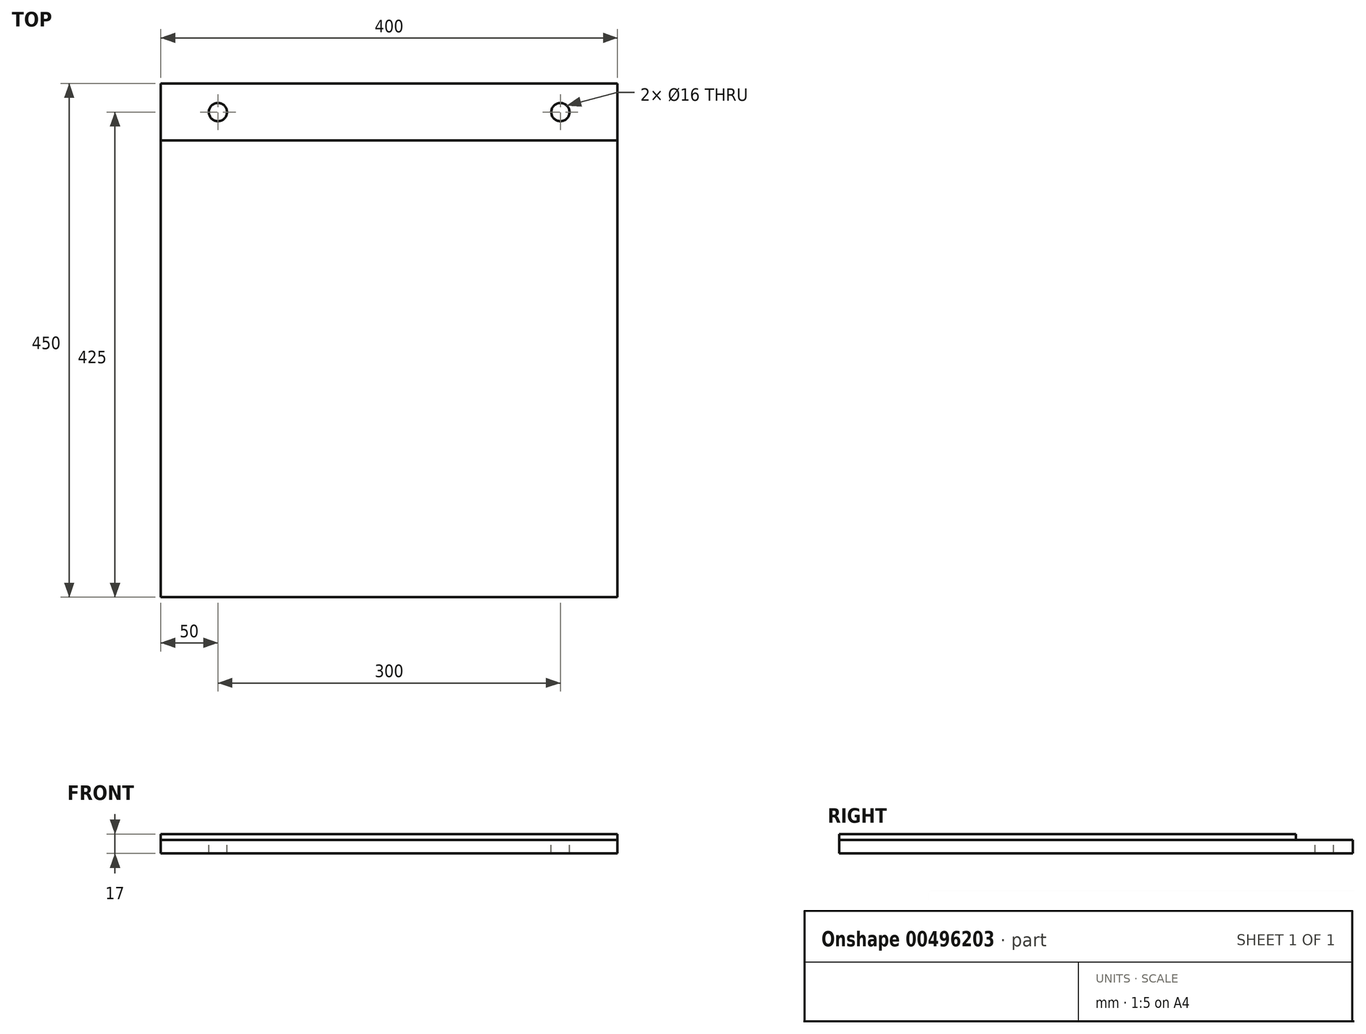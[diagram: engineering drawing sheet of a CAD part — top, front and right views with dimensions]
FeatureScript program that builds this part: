
annotation { "Feature Type Name" : "Feature", "Feature Type Description" : "" }
export const myFeature = defineFeature(function(context is Context, id is Id, definition is map)
    precondition{}
    {
        {
            var Q0;
            Q0=qCreatedBy(makeId("Top.planeOp"),FACE);
            var sketch = newSketch(context, id + "F0", { "sketchPlane" : qUnion([Q0])});
            skLineSegment(sketch, "E0.bottom", {"start": v(0, 0) * mm, "end": v(-400, 0) * mm});
            skLineSegment(sketch, "E0.top", {"start": v(0, 400) * mm, "end": v(-400, 400) * mm});
            skLineSegment(sketch, "E0.left", {"start": v(0, 0) * mm, "end": v(0, 400) * mm});
            skLineSegment(sketch, "E0.right", {"start": v(-400, 0) * mm, "end": v(-400, 400) * mm});
            skSolve(sketch);
        }
        {
            var Q0;
            Q0=makeQuery(id+"F0.imprint","IMPRINT",FACE,{"disambiguationData":[TD([[makeQuery(id+"F0.imprint","IMPRINT",EDGE,{"derivedFrom":sQuery(id+"F0.wireOp",EDGE,"E0.bottom")}),-1.0]])]});
            extrude(context, id + "F1", {"entities" : qUnion([Q0]), "depth" : 5 * mm});
        }
        {
            var Q0;
            Q0=makeQuery(id+"F1.opExtrude","CAP_FACE",FACE,{"disambiguationData":[OSD([sQuery(id+"F0.wireOp",EDGE,"E0.bottom"),sQuery(id+"F0.wireOp",EDGE,"E0.top"),sQuery(id+"F0.wireOp",EDGE,"E0.left"),sQuery(id+"F0.wireOp",EDGE,"E0.right")])],"isStart":true});
            var sketch = newSketch(context, id + "F2", { "sketchPlane" : qUnion([Q0])});
            skLineSegment(sketch, "E1.top", {"start": v(0, -450) * mm, "end": v(-400, -450) * mm});
            skLineSegment(sketch, "E1.left", {"start": v(0, -400) * mm, "end": v(0, -450) * mm});
            skLineSegment(sketch, "E1.right", {"start": v(-400, -400) * mm, "end": v(-400, -450) * mm});
            skLineSegment(sketch, "E2", {"start": v(-400, -425) * mm, "end": v(0, -425) * mm, "construction": true});
            skLineSegment(sketch, "E3", {"start": v(-350, -450) * mm, "end": v(-350, -400) * mm, "construction": true});
            skLineSegment(sketch, "E4", {"start": v(-50, -450) * mm, "end": v(-50, -400) * mm, "construction": true});
            skCircle(sketch, "E5", {"center": v(-350, -425) * mm, "radius": 8 * mm});
            skCircle(sketch, "E6", {"center": v(-50, -425) * mm, "radius": 8 * mm});
            skLineSegment(sketch, "E7", {"start": v(0, -400) * mm, "end": v(0, 0) * mm});
            skLineSegment(sketch, "E8", {"start": v(0, 0) * mm, "end": v(-400, 0) * mm});
            skLineSegment(sketch, "E9", {"start": v(-400, 0) * mm, "end": v(-400, -400) * mm});
            skSolve(sketch);
        }
        {
            var Q0;
            Q0=makeQuery(id+"F2.imprint","IMPRINT",FACE,{"disambiguationData":[TD([[makeQuery(id+"F2.imprint","IMPRINT",EDGE,{"derivedFrom":sQuery(id+"F2.wireOp",EDGE,"E1.top")}),-1.0]])]});
            var Q1;
            Q1=makeQuery(id+"F2.imprint","IMPRINT",FACE,{"disambiguationData":[TD([[makeQuery(id+"F2.imprint","IMPRINT",EDGE,{"derivedFrom":sQuery(id+"F2.wireOp",EDGE,"E7")}),-1.0]])]});
            extrude(context, id + "F3", {"entities" : qUnion([Q0, Q1]), "depth" : 12 * mm});
        }
    });
